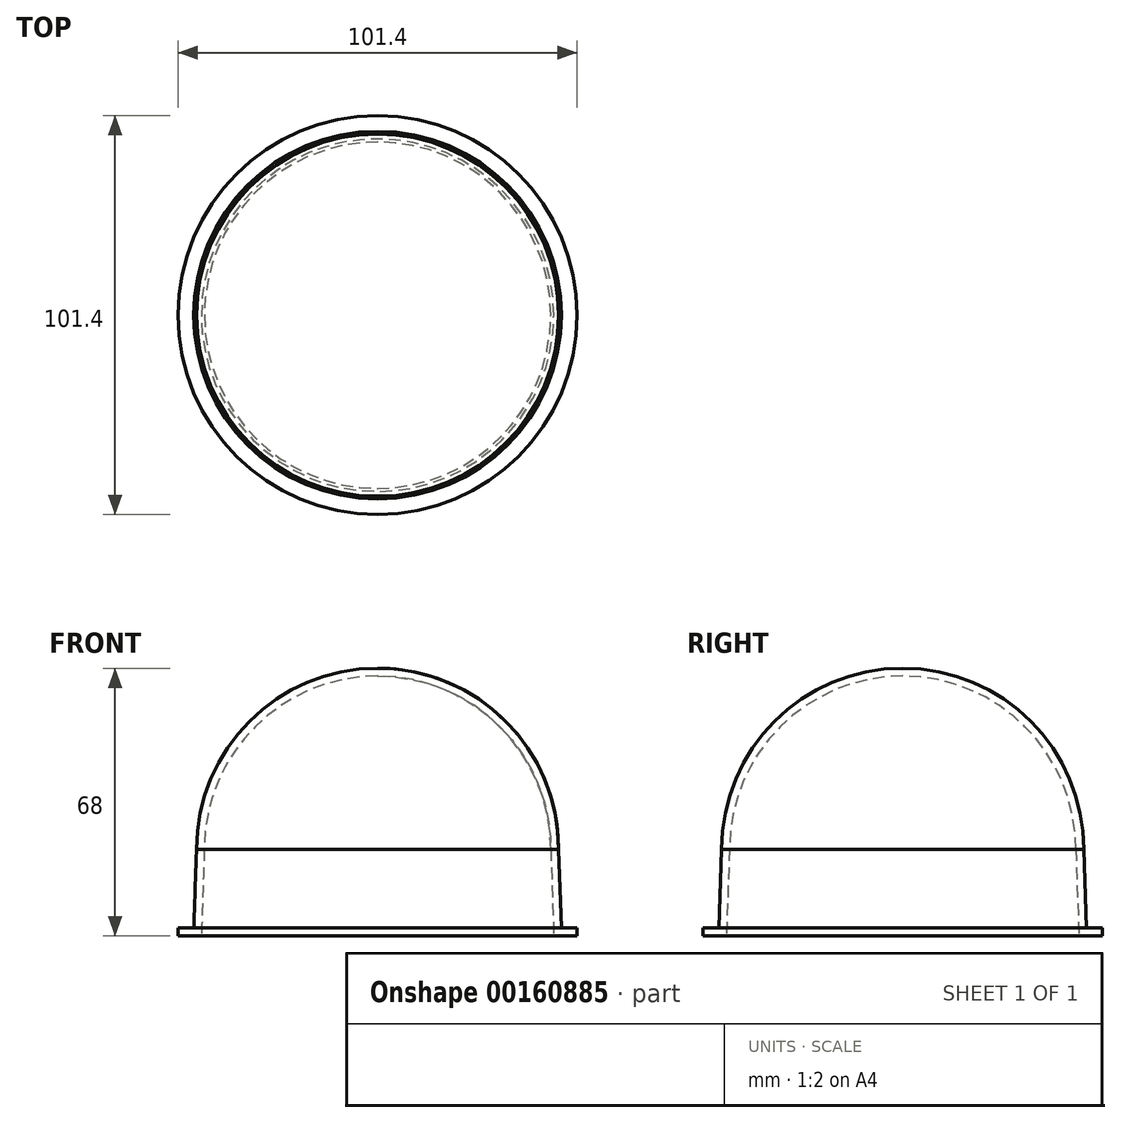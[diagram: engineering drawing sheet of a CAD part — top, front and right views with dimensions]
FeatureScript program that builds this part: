
annotation { "Feature Type Name" : "Feature", "Feature Type Description" : "" }
export const myFeature = defineFeature(function(context is Context, id is Id, definition is map)
    precondition{}
    {
        {
            var Q0;
            Q0=qCreatedBy(makeId("Front.planeOp"),FACE);
            var sketch = newSketch(context, id + "F0", { "sketchPlane" : qUnion([Q0])});
            skArc(sketch, "E0", {"start": v(44, 0) * mm, "mid": v(31.11, 31.11) * mm, "end": v(0, 44) * mm});
            skLineSegment(sketch, "E1", {"start": v(-44, 0) * mm, "end": v(44, 0) * mm, "construction": true});
            skArc(sketch, "E2.1", {"start": v(46, 0) * mm, "mid": v(32.53, 32.53) * mm, "end": v(0, 46) * mm});
            skLineSegment(sketch, "E3", {"start": v(0, -15.9) * mm, "end": v(0, 56) * mm, "construction": true});
            skLineSegment(sketch, "E4", {"start": v(46, 0) * mm, "end": v(46.7, -20) * mm});
            skLineSegment(sketch, "E5", {"start": v(44, 0) * mm, "end": v(44.7, -20) * mm});
            skLineSegment(sketch, "E6", {"start": v(44.7, -20) * mm, "end": v(44.77, -22) * mm});
            skLineSegment(sketch, "E7", {"start": v(44.77, -22) * mm, "end": v(50.7, -22) * mm});
            skLineSegment(sketch, "E8", {"start": v(50.7, -22) * mm, "end": v(50.7, -20) * mm});
            skLineSegment(sketch, "E9", {"start": v(50.7, -20) * mm, "end": v(46.7, -20) * mm});
            skLineSegment(sketch, "E10", {"start": v(0, 46) * mm, "end": v(0, 44) * mm});
            skSolve(sketch);
        }
        {
            var Q0;
            Q0 = qSketchRegion(id + "F0", true);
            var Q1;
            Q1=sQuery(id+"F0.wireOp",EDGE,"E3");
            revolve(context, id + "F1", {"entities" : qUnion([Q0]), "axis" : qUnion([Q1]), "revolveType" : RevolveType.FULL});
        }
    });
